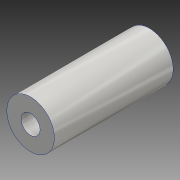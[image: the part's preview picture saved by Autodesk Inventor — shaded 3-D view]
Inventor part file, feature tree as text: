
AUTODESK INVENTOR PART (.ipt)
format: ipt  version: 2016 (Build 200138000, 138)  size: 122,880 bytes
history: native  units: mm
features: extrude x2, sketch x2
ambient origin geometry x8: Origin, YZ Plane, XZ Plane, XY Plane, X Axis, Y Axis, Z Axis, Center Point
bodies: 实体1 (feature_tree)
feature tree (4):
  extrude  "拉伸1"  Depth=25.0mm TaperAngle=0.0deg
  extrude  "拉伸3"  Depth=3.0mm TaperAngle=0.0deg
  sketch  "草图1"  dims[d0=10.0mm d2=25.0mm d3=0.0mm]
  sketch  "草图3"  dims[d7=4.0mm d8=3.0mm d9=0.0mm]
